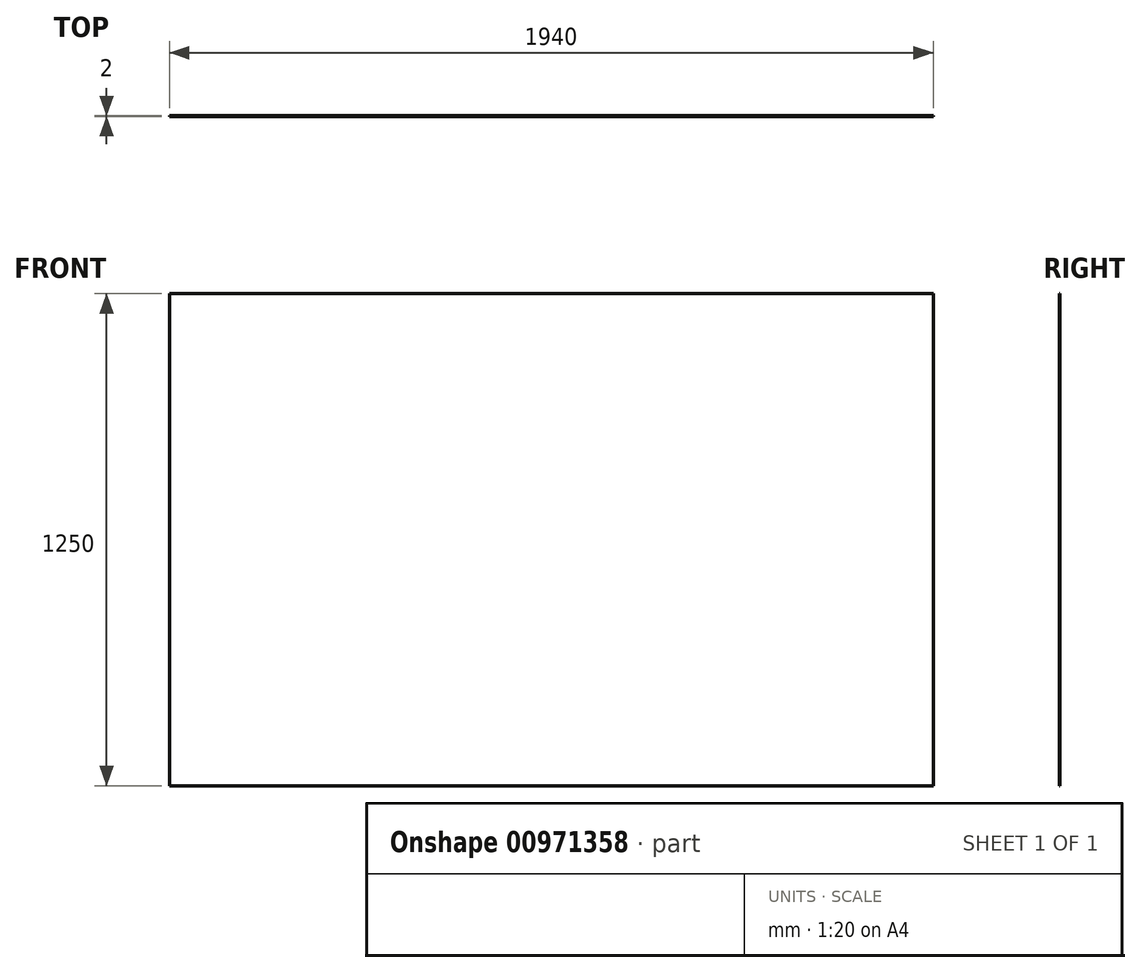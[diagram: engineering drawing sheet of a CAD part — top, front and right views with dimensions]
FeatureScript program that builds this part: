
annotation { "Feature Type Name" : "Feature", "Feature Type Description" : "" }
export const myFeature = defineFeature(function(context is Context, id is Id, definition is map)
    precondition{}
    {
        {
            var Q0;
            Q0=qCreatedBy(makeId("Front.planeOp"),FACE);
            var sketch = newSketch(context, id + "F0", { "sketchPlane" : qUnion([Q0])});
            skLineSegment(sketch, "E0.bottom", {"start": v(970, 625) * mm, "end": v(-970, 625) * mm});
            skLineSegment(sketch, "E0.top", {"start": v(970, -625) * mm, "end": v(-970, -625) * mm});
            skLineSegment(sketch, "E0.left", {"start": v(970, 625) * mm, "end": v(970, -625) * mm});
            skLineSegment(sketch, "E0.right", {"start": v(-970, 625) * mm, "end": v(-970, -625) * mm});
            skPoint(sketch, "E0.middle", {"position": v(0, 0) * mm});
            skSolve(sketch);
        }
        {
            var Q0;
            Q0=makeQuery(id+"F0.imprint","IMPRINT",FACE,{"disambiguationData":[TD([[makeQuery(id+"F0.imprint","IMPRINT",EDGE,{"derivedFrom":sQuery(id+"F0.wireOp",EDGE,"E0.bottom")}),1.0]])]});
            extrude(context, id + "F1", {"entities" : qUnion([Q0]), "depth" : 2 * mm, "offsetDistance" : 25 * mm});
        }
    });
